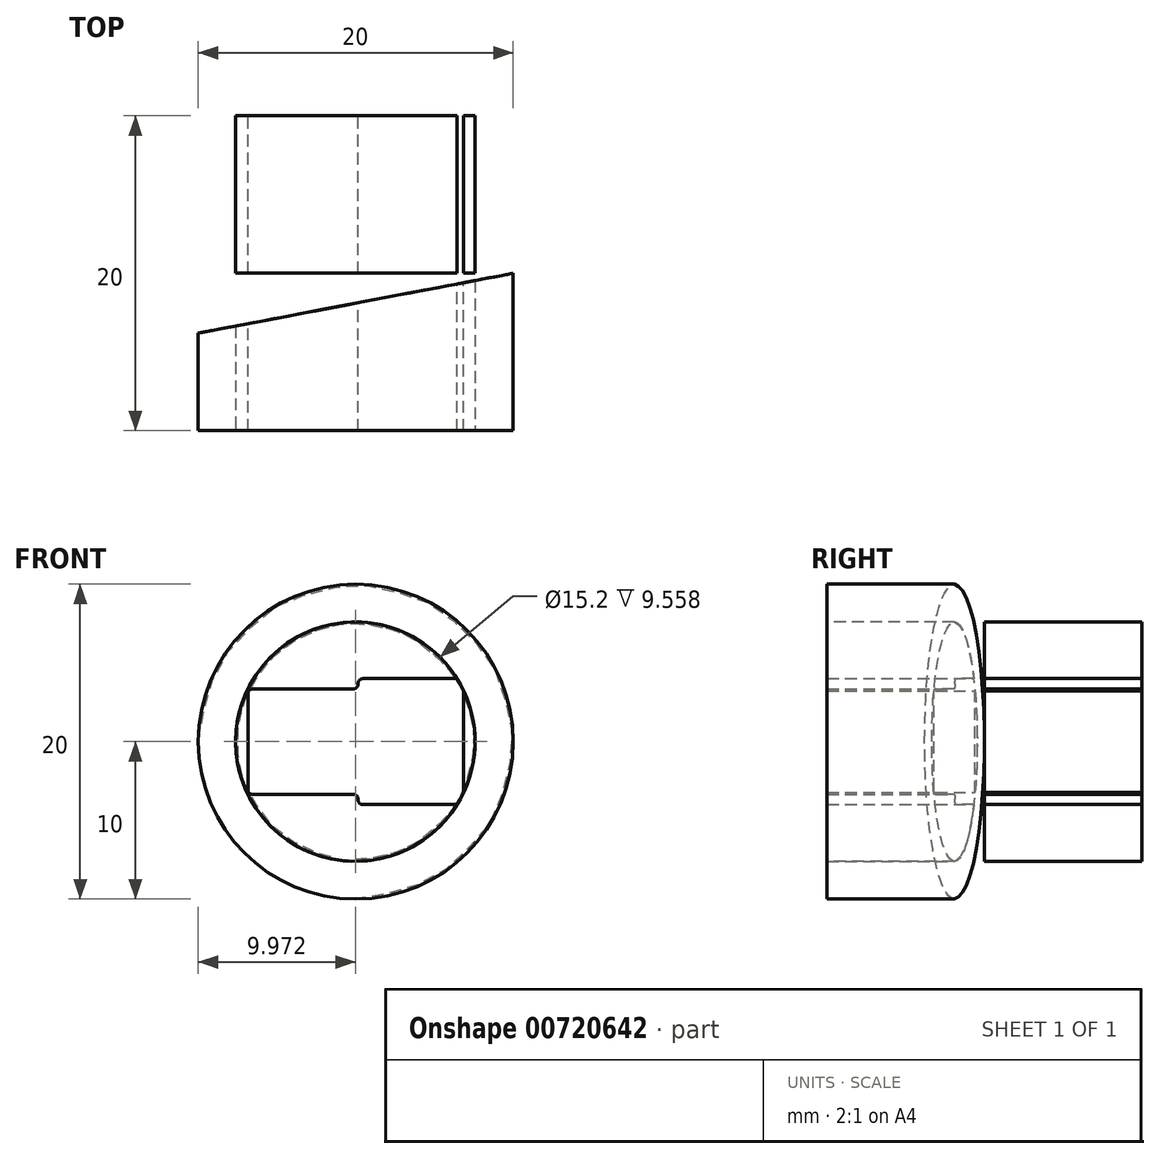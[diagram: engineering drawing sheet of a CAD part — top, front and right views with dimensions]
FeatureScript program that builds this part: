
annotation { "Feature Type Name" : "Feature", "Feature Type Description" : "" }
export const myFeature = defineFeature(function(context is Context, id is Id, definition is map)
    precondition{}
    {
        {
            var Q0;
            Q0=qCreatedBy(makeId("Front.planeOp"),FACE);
            var sketch = newSketch(context, id + "F0", { "sketchPlane" : qUnion([Q0])});
            skLineSegment(sketch, "E0.bottom", {"start": v(-6.85, 3.35) * mm, "end": v(0.15, 3.35) * mm});
            skLineSegment(sketch, "E0.top", {"start": v(-6.85, -3.35) * mm, "end": v(0.15, -3.35) * mm});
            skLineSegment(sketch, "E0.left", {"start": v(-6.85, 3.35) * mm, "end": v(-6.85, -3.35) * mm});
            skLineSegment(sketch, "E0.right", {"start": v(0.15, 3.35) * mm, "end": v(0.15, -3.35) * mm});
            skLineSegment(sketch, "E1.bottom", {"start": v(0.15, 4) * mm, "end": v(6.85, 4) * mm});
            skLineSegment(sketch, "E1.top", {"start": v(0.15, -4) * mm, "end": v(6.85, -4) * mm});
            skLineSegment(sketch, "E1.left", {"start": v(0.15, 4) * mm, "end": v(0.15, -4) * mm});
            skLineSegment(sketch, "E1.right", {"start": v(6.85, 4) * mm, "end": v(6.85, -4) * mm});
            skPoint(sketch, "E2", {"position": v(0.15, 0) * mm});
            skLineSegment(sketch, "E3", {"start": v(6.85, 0) * mm, "end": v(-6.85, 0) * mm, "construction": true});
            skPoint(sketch, "E4", {"position": v(0, 0) * mm});
            skSolve(sketch);
        }
        {
            var Q0;
            Q0=makeQuery(id+"F0.imprint","IMPRINT",FACE,{"disambiguationData":[TD([[makeQuery(id+"F0.imprint","IMPRINT",EDGE,{"derivedFrom":sQuery(id+"F0.wireOp",EDGE,"E0.bottom")}),-1.0]])]});
            var Q1;
            {var subQ1=sQuery(id+"F0.wireOp",EDGE,"E0.right");Q1=makeQuery(id+"F0.imprint","IMPRINT",FACE,{"disambiguationData":[TD([[makeQuery(id+"F0.imprint","IMPRINT",EDGE,{"derivedFrom":subQ1}),1.0]])]});}
            extrude(context, id + "F1", {"entities" : qUnion([Q0, Q1]), "depth" : 40 * mm, "offsetDistance" : 25 * mm});
        }
        {
            var Q0;
            Q0=makeQuery(id+"F1.opExtrude","SWEPT_EDGE",EDGE,{"disambiguationData":[OSD([sQuery(id+"F0.wireOp",EDGE,"E0.bottom"),sQuery(id+"F0.wireOp",EDGE,"E0.left")])]});
            var Q1;
            Q1=makeQuery(id+"F1.opExtrude","SWEPT_EDGE",EDGE,{"disambiguationData":[OSD([sQuery(id+"F0.wireOp",EDGE,"E0.bottom"),sQuery(id+"F0.wireOp",EDGE,"E0.right"),sQuery(id+"F0.wireOp",EDGE,"E1.left")])]});
            var Q2;
            Q2=makeQuery(id+"F1.opExtrude","SWEPT_EDGE",EDGE,{"disambiguationData":[OSD([sQuery(id+"F0.wireOp",EDGE,"E1.bottom"),sQuery(id+"F0.wireOp",EDGE,"E1.left")])]});
            var Q3;
            Q3=makeQuery(id+"F1.opExtrude","SWEPT_EDGE",EDGE,{"disambiguationData":[OSD([sQuery(id+"F0.wireOp",EDGE,"E1.bottom"),sQuery(id+"F0.wireOp",EDGE,"E1.right")])]});
            var Q4;
            Q4=makeQuery(id+"F1.opExtrude","SWEPT_EDGE",EDGE,{"disambiguationData":[OSD([sQuery(id+"F0.wireOp",EDGE,"E0.top"),sQuery(id+"F0.wireOp",EDGE,"E0.left")])]});
            var Q5;
            Q5=makeQuery(id+"F1.opExtrude","SWEPT_EDGE",EDGE,{"disambiguationData":[OSD([sQuery(id+"F0.wireOp",EDGE,"E0.top"),sQuery(id+"F0.wireOp",EDGE,"E0.right"),sQuery(id+"F0.wireOp",EDGE,"E1.left")])]});
            var Q6;
            Q6=makeQuery(id+"F1.opExtrude","SWEPT_EDGE",EDGE,{"disambiguationData":[OSD([sQuery(id+"F0.wireOp",EDGE,"E1.top"),sQuery(id+"F0.wireOp",EDGE,"E1.left")])]});
            var Q7;
            Q7=makeQuery(id+"F1.opExtrude","SWEPT_EDGE",EDGE,{"disambiguationData":[OSD([sQuery(id+"F0.wireOp",EDGE,"E1.top"),sQuery(id+"F0.wireOp",EDGE,"E1.right")])]});
            fillet(context, id + "F2", {"entities" : qUnion([Q0, Q1, Q2, Q3, Q4, Q5, Q6, Q7]), "tangentPropagation" : true, "radius" : 0.3 * mm, "defaultsChanged" : true, "vertexSettings" : [], "allowEdgeOverflow" : false});
        }
        {
            var Q0;
            Q0=qCreatedBy(makeId("Front.planeOp"),FACE);
            var sketch = newSketch(context, id + "F3", { "sketchPlane" : qUnion([Q0])});
            skCircle(sketch, "E5", {"center": v(-0.03, 0) * mm, "radius": 7.6 * mm});
            skSolve(sketch);
        }
        {
            var Q0;
            Q0 = qSketchRegion(id + "F3", true);
            extrude(context, id + "F4", {"entities" : qUnion([Q0]), "depth" : 20 * mm, "offsetDistance" : 25 * mm});
        }
        {
            var Q0;
            Q0=makeQuery(id+"F4.opExtrude","CAP_FACE",FACE,{"disambiguationData":[OSD([sQuery(id+"F3.wireOp",EDGE,"E5")])],"isStart":false});
            var sketch = newSketch(context, id + "F5", { "sketchPlane" : qUnion([Q0])});
            skCircle(sketch, "E6", {"center": v(0, 0) * mm, "radius": 10 * mm});
            skSolve(sketch);
        }
        {
            var Q0;
            Q0=makeQuery(id+"F5.imprint","IMPRINT",FACE,{"disambiguationData":[TD([[makeQuery(id+"F5.imprint","IMPRINT",EDGE,{"derivedFrom":sQuery(id+"F5.wireOp",EDGE,"E6")}),1.0]])]});
            extrude(context, id + "F6", {"entities" : qUnion([Q0]), "oppositeDirection" : true, "depth" : 10 * mm, "offsetDistance" : 25 * mm});
        }
        {
            var Q0;
            Q0=makeQuery(id+"F1.opExtrude","SWEPT_BODY",BODY,{"disambiguationData":[OSD([sQuery(id+"F0.wireOp",EDGE,"E0.bottom"),sQuery(id+"F0.wireOp",EDGE,"E0.top"),sQuery(id+"F0.wireOp",EDGE,"E0.left"),sQuery(id+"F0.wireOp",EDGE,"E1.bottom"),sQuery(id+"F0.wireOp",EDGE,"E1.top"),sQuery(id+"F0.wireOp",EDGE,"E1.left"),sQuery(id+"F0.wireOp",EDGE,"E1.right")])]});
            var Q1;
            Q1=makeQuery(id+"F4.opExtrude","SWEPT_BODY",BODY,{"disambiguationData":[OSD([sQuery(id+"F3.wireOp",EDGE,"E5")])]});
            booleanBodies(context, id + "F7", {"operationType" : BooleanOperationType.SUBTRACTION, "tools" : qUnion([Q0]), "targets" : qUnion([Q1])});
        }
        {
            var Q0;
            Q0=qCreatedBy(makeId("Top.planeOp"),FACE);
            var sketch = newSketch(context, id + "F8", { "sketchPlane" : qUnion([Q0])});
            skLineSegment(sketch, "E7", {"start": v(-10, -10) * mm, "end": v(10, -10) * mm});
            skLineSegment(sketch, "E8", {"start": v(10, -10) * mm, "end": v(10, -10) * mm});
            skLineSegment(sketch, "E9", {"start": v(10, -10) * mm, "end": v(-10, -13.8) * mm});
            skLineSegment(sketch, "E10", {"start": v(-10, -13.8) * mm, "end": v(-10, -10) * mm});
            skSolve(sketch);
        }
        {
            var Q0;
            Q0 = qSketchRegion(id + "F8", true);
            extrude(context, id + "F9", {"entities" : qUnion([Q0]), "operationType" : NewBodyOperationType.REMOVE, "endBound" : BoundingType.THROUGH_ALL, "oppositeDirection" : true, "depth" : 25 * mm, "offsetDistance" : 25 * mm, "hasSecondDirection" : true, "secondDirectionBound" : BoundingType.THROUGH_ALL, "secondDirectionOppositeDirection" : false, "secondDirectionDepth" : 25 * mm});
        }
    });
